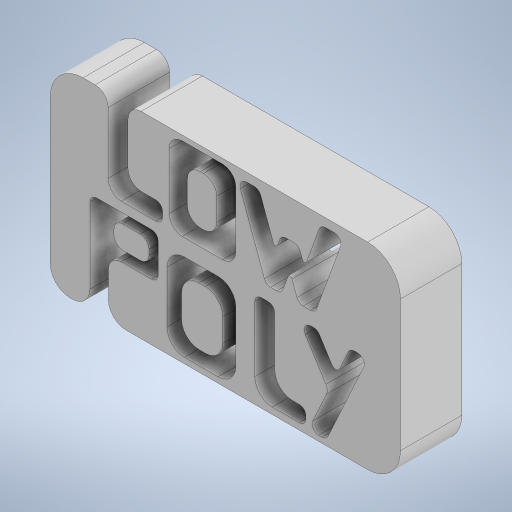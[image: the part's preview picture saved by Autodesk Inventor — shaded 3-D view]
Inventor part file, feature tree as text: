
AUTODESK INVENTOR PART (.ipt)
format: ipt  version: 2024.1 (Build 281209000, 209)  size: 712,704 bytes
history: native  units: mm
features: fillet x36, sketch x4, extrude x3, projected_geometry x1
ambient origin geometry x8: Origin, YZ Plane, XZ Plane, XY Plane, X Axis, Y Axis, Z Axis, Center Point
bodies: Solid2 (feature_tree)
feature tree (44):
  extrude  "Extrusion6"  Depth=10.0mm TaperAngle=0.0deg
  extrude  "Extrusion1"  Depth=90.0mm
  extrude  "Extrusion7"  Depth=3.0mm
  fillet  "Fillet24"  Radius=19.198622mm
  fillet  "Fillet25"  Radius=10.0mm
  fillet  "Fillet26"  Radius=28.0mm
  fillet  "Fillet27"  [1 undecoded]
  fillet  "Fillet28"  Radius=4.0mm
  fillet  "Fillet29"  Radius=5.0mm
  fillet  "Fillet30"  Radius=5.0mm
  fillet  "Fillet31"  Radius=10.0mm
  fillet  "Fillet32"  Radius=10.0mm
  fillet  "Fillet33"  Radius=5.0mm
  fillet  "Fillet34"  Radius=3.5mm
  fillet  "Fillet35"  Radius=3.0mm
  fillet  "Fillet36"  Radius=6.0mm
  fillet  "Fillet1"  Radius=3.5mm
  fillet  "Fillet2"  Radius=3.5mm
  fillet  "Fillet3"  Radius=4.0mm
  fillet  "Fillet4"  Radius=4.0mm
  fillet  "Fillet5"  Radius=7.0mm
  fillet  "Fillet6"  Radius=6.0mm
  fillet  "Fillet7"  Radius=6.0mm
  fillet  "Fillet8"  Radius=5.0mm
  fillet  "Fillet9"  Radius=4.0mm
  fillet  "Fillet10"  Radius=1.0mm
  fillet  "Fillet11"  Radius=3.0mm
  fillet  "Fillet12"  Radius=3.0mm
  fillet  "Fillet13"  Radius=19.198622mm
  fillet  "Fillet14"  Radius=7.056118mm
  fillet  "Fillet15"  Radius=7.5mm
  fillet  "Fillet16"  Radius=6.0mm
  fillet  "Fillet17"  Radius=3.0mm
  fillet  "Fillet18"  Radius=3.931055mm
  fillet  "Fillet19"  Radius=3.9mm
  fillet  "Fillet20"  Radius=3.0mm
  fillet  "Fillet21"  Radius=6.0mm
  fillet  "Fillet22"  Radius=6.0mm
  fillet  "Fillet23"  Radius=3.0mm
  sketch  "Sketch8"  dims[d75=1.0mm d76=3.0mm d77=8.0mm d78=8.0mm d79=4.0mm d80=2.0mm d81=6.0mm d82=15.0mm d83=9.0mm d84=0.0mm d85=0.0mm d86=0.0mm d87=0.0mm]
  sketch  "Sketch1"  dims[d0=40.0mm d4=10.0mm d5=0.0mm]
  sketch  "Sketch6"  dims[d24=160.0mm d25=90.0mm]
  projected_geometry  "Projected Loop1"
  sketch  "Sketch7"  dims[d26=90.0mm d27=0.0mm d28=19.198622mm d29=19.198622mm d31=10.0mm d39=28.0mm d40=0.0mm d41=0.0mm d42=4.0mm d43=5.0mm d44=5.0mm d45=10.0mm d46=10.0mm d47=5.0mm d48=3.5mm d49=3.0mm d50=6.0mm d51=3.5mm d52=3.5mm d53=4.0mm d54=4.0mm d55=7.0mm d56=6.0mm d57=6.0mm d58=5.0mm d59=4.0mm d60=1.0mm d61=3.0mm d62=3.0mm d63=19.198622mm d64=7.056118mm d65=7.5mm d66=6.0mm d67=3.0mm d69=3.931055mm d70=3.9mm d71=3.0mm d72=6.0mm d73=6.0mm d74=3.0mm]
note: 1 required parameter value undecoded (feature->parameter linkage not recoverable at this tier; creation-order binding heuristic only, values carry confidence <= 0.55)
